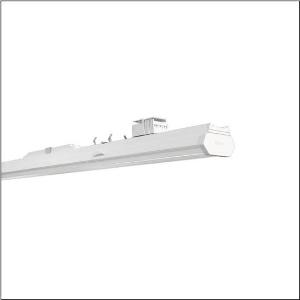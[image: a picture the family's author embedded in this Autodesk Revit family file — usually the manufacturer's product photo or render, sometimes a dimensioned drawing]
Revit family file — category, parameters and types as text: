
# Revit family: licross_r__21_protected_mo_52td1b7n48xg_600d
name_source: partatom
category: Lighting Fixtures
units: mm (PartAtom-declared; Revit-internal decimal feet)

## family parameters
Cut with Voids When Loaded = No
Host = Face
Light Source = No
Part Type = Normal
Room Calculation Point = No
Round Connector Dimension = Use Diameter
Shared = No

## types (1)
- Licross® 21 Protected MO (1 x LED, 8090 lm, 47.9 W, 4000K)
    Apparent Load = 48 VA
    CIE Flux Codes = 54 82 95 97 100
    Color Rendering = 80
    Color Temperature = 4000K
    Default Elevation = 1800 mm
    Description = Licross® 21 Protected MO, luminaire insert, of sheet steel, galvanised, coil coated, white, length: 1.500mm, width: 90mm, height: 103mm, LED rated luminous flux: 8.090lm, light colour: 840, control gear: ON/OFF, with plug, 3-pole, with phase selection, mains connection: 220..240V, AC, 50/60Hz, rated input power: 48W, halogen-free wiring, primary optical cover: cover, of PMMA, light emission: direct distribution, primary light characteristic: symmetric, protection rating (complete): IP54, insulation class (complete): insulation class I (protective earthing), certification: CE, ENEC, VDE, UKCA, protection symbol: D if used in an environment with non-conductive dust loads with corresponding accessories, impact resistance: IK06, permissible ambient temperature for indoor applications: -35..+45°C, corresponds to IFS (International Featured Standards) requirements for safety and quality in the food industry, reducing of maximum allowable ambient temperature of 5°C with ceiling mounting, LABS conformity tested according to VDMA 24364:2018-05, packaging unit: 1 piece
    Height = 92 mm
    Lamp = 1 x LED
    Lamp Light Flux = 8090 lm
    Lamp Power = 47.9 W
    Lamp count = 1
    Length = 1500 mm
    Luminous efficacy = 169 lm/W
    Manufacturer = Siteco
    ModVariant = No
    Model = 52TD1B7N48XG
    Mounting Place = Ceiling
    Mounting Type = Pendant
    Number of Poles = 1
    OnlyDefault = Yes
    Power Factor = 1
    Product Name = Licross® 21 Protected MO
    Product group = luminaire insert
    ProductGroupID = 901
    Protection Class = Protection class I
    Protection Degree = IP 54
    RLX_Detail_Level = 1
    RLX_Emergency_Light_Flux = 0 lm
    RLX_Emergency_Type = 0
    RLX_Emergency_Type_DB = No
    RlxData = <blob elided: 20613 chars, md5=45f7daa6>
    Socket = socket
    Standby Power = 0 W
    System Light Flux = 8090 lm
    System Power = 48 W
    Type Comments = Product without accessories
    Type Image = l_1256148.jpg
    URL = http://relux.com
    VarID = ---
    Voltage = 0 V
    Weight = 0.00 kg
    Width = 88 mm

## geometry (parser evidence)
native form markers: Blend x4, Sweep x11
no freeform markers — native parametric forms only
